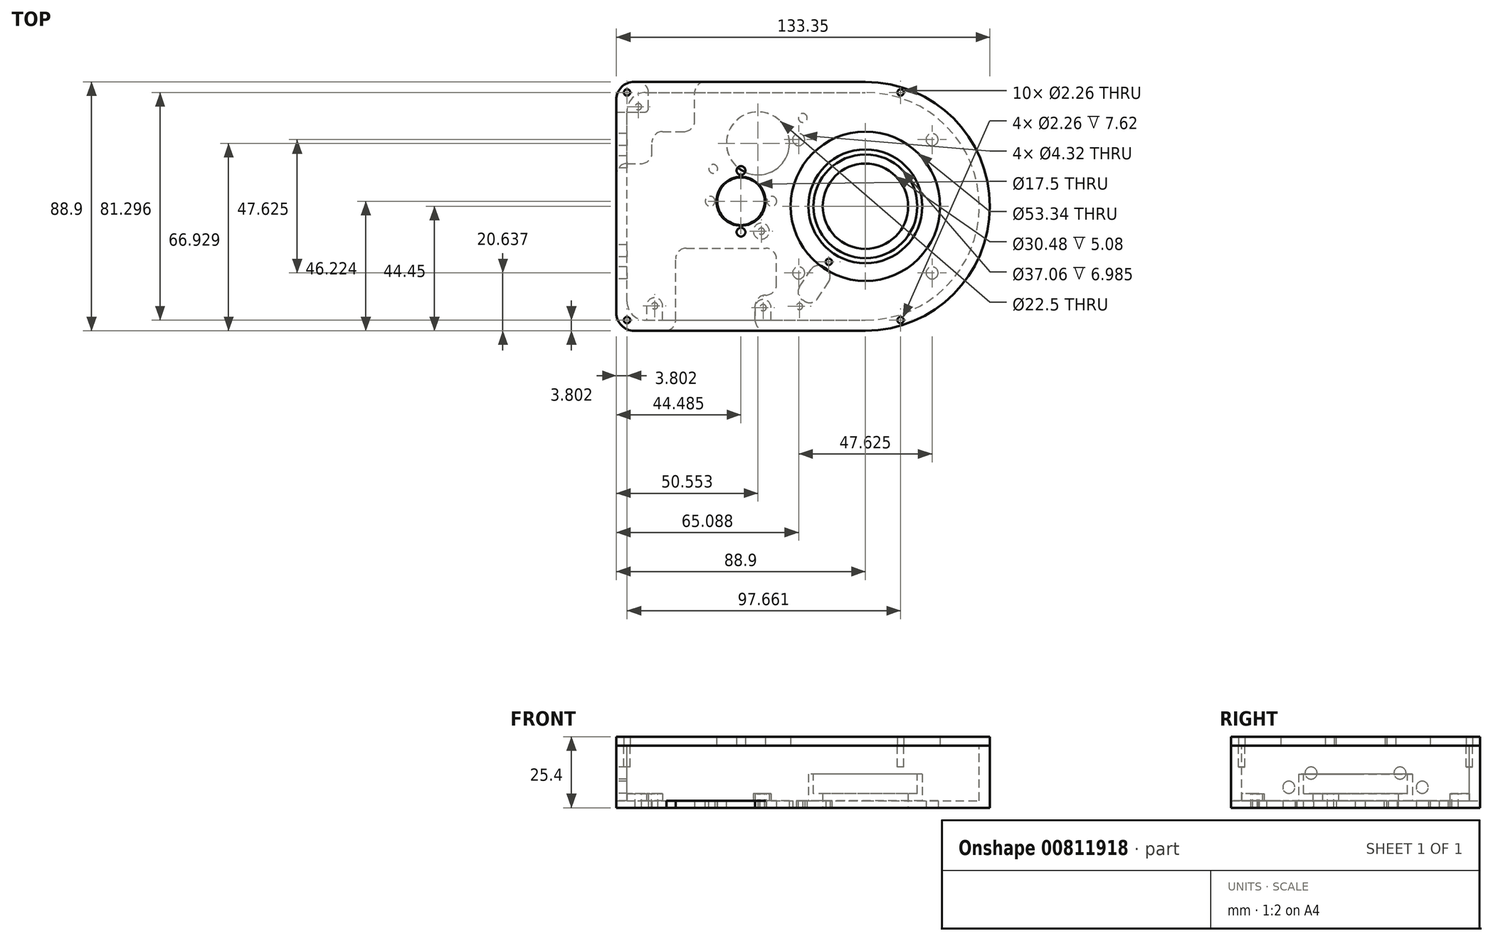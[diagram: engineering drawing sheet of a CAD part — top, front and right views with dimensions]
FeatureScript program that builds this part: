
annotation { "Feature Type Name" : "Feature", "Feature Type Description" : "" }
export const myFeature = defineFeature(function(context is Context, id is Id, definition is map)
    precondition{}
    {
        {
            var Q0;
            Q0=qCreatedBy(makeId("Top.planeOp"),FACE);
            var sketch = newSketch(context, id + "F0", { "sketchPlane" : qUnion([Q0])});
            skLineSegment(sketch, "E0.bottom", {"start": v(6.35, 0) * mm, "end": v(88.9, 0) * mm});
            skLineSegment(sketch, "E0.top", {"start": v(6.35, 88.9) * mm, "end": v(88.9, 88.9) * mm});
            skLineSegment(sketch, "E0.left", {"start": v(0, 6.35) * mm, "end": v(0, 82.55) * mm});
            skArc(sketch, "E1", {"start": v(88.9, 0) * mm, "mid": v(133.35, 44.45) * mm, "end": v(88.9, 88.9) * mm});
            skCircle(sketch, "E2", {"center": v(88.9, 44.45) * mm, "radius": 15.24 * mm});
            skPoint(sketch, "E3.visualSharp", {"position": v(0, 88.9) * mm});
            skArc(sketch, "E3.filletArc", {"start": v(6.35, 88.9) * mm, "mid": v(1.86, 87.04) * mm, "end": v(0, 82.55) * mm});
            skPoint(sketch, "E4.visualSharp", {"position": v(0, 0) * mm});
            skArc(sketch, "E4.filletArc", {"start": v(0, 6.35) * mm, "mid": v(1.86, 1.86) * mm, "end": v(6.35, 0) * mm});
            skSolve(sketch);
        }
        {
            var Q0;
            {var subQ4=sQuery(id+"F0.wireOp",EDGE,"E1");var subQ7=sQuery(id+"F0.wireOp",EDGE,"E0.bottom");Q0=qUnion([makeQuery(id+"F0.imprint","IMPRINT",FACE,{"disambiguationData":[TD([[makeQuery(id+"F0.imprint","IMPRINT",EDGE,{"derivedFrom":subQ7}),1.0]])]}),makeQuery(id+"F0.imprint","IMPRINT",FACE,{"disambiguationData":[TD([[makeQuery(id+"F0.imprint","IMPRINT",EDGE,{"derivedFrom":subQ4}),1.0]])]})]);}
            extrude(context, id + "F1", {"entities" : qUnion([Q0]), "depth" : 22.22 * mm});
        }
        {
            var Q0;
            Q0=makeQuery(id+"F1.opExtrude","CAP_FACE",FACE,{"disambiguationData":[OSD([sQuery(id+"F0.wireOp",EDGE,"E0.bottom"),sQuery(id+"F0.wireOp",EDGE,"E0.top"),sQuery(id+"F0.wireOp",EDGE,"E0.left"),sQuery(id+"F0.wireOp",EDGE,"E1"),sQuery(id+"F0.wireOp",EDGE,"E2")])],"isStart":false});
            var sketch = newSketch(context, id + "F2", { "sketchPlane" : qUnion([Q0])});
            skLineSegment(sketch, "E5.0", {"start": v(10.41, 85.1) * mm, "end": v(88.9, 85.1) * mm});
            skLineSegment(sketch, "E5.1", {"start": v(3.8, 10.41) * mm, "end": v(3.8, 78.49) * mm});
            skLineSegment(sketch, "E5.2", {"start": v(10.41, 3.8) * mm, "end": v(88.9, 3.8) * mm});
            skArc(sketch, "E5.3", {"start": v(88.9, 3.81) * mm, "mid": v(129.54, 44.45) * mm, "end": v(88.9, 85.1) * mm});
            skPoint(sketch, "E6.visualSharp", {"position": v(3.8, 85.1) * mm});
            skArc(sketch, "E6.filletArc", {"start": v(10.41, 85.1) * mm, "mid": v(5.74, 83.16) * mm, "end": v(3.8, 78.49) * mm});
            skPoint(sketch, "E7.visualSharp", {"position": v(3.8, 3.8) * mm});
            skArc(sketch, "E7.filletArc", {"start": v(3.8, 10.41) * mm, "mid": v(5.74, 5.74) * mm, "end": v(10.41, 3.8) * mm});
            skSolve(sketch);
        }
        {
            var Q0;
            {var subQ0=makeQuery(id+"F2.imprint","IMPRINT",EDGE,{"derivedFrom":makeQuery(id+"F1.opExtrude","CAP_EDGE",EDGE,{"disambiguationData":[OSD([sQuery(id+"F0.wireOp",EDGE,"E2")])],"isStart":false})});Q0=qUnion([makeQuery(id+"F2.imprint","IMPRINT",FACE,{"disambiguationData":[TD([[subQ0,1.0]])]}),makeQuery(id+"F2.imprint","IMPRINT",FACE,{"disambiguationData":[TD([[makeQuery(id+"F2.imprint","IMPRINT",EDGE,{"derivedFrom":sQuery(id+"F2.wireOp",EDGE,"E5.0")}),-1.0]])]})]);}
            extrude(context, id + "F3", {"entities" : qUnion([Q0]), "operationType" : NewBodyOperationType.REMOVE, "oppositeDirection" : true, "depth" : 19.68 * mm});
        }
        {
            var Q0;
            Q0=makeQuery(id+"F3.boolean.opBoolean","COPY",FACE,{"derivedFrom":makeQuery(id+"F3.opExtrude","CAP_FACE",FACE,{"disambiguationData":[OSD([sQuery(id+"F2.wireOp",EDGE,"E5.0"),sQuery(id+"F2.wireOp",EDGE,"E5.1"),sQuery(id+"F2.wireOp",EDGE,"E5.2"),sQuery(id+"F2.wireOp",EDGE,"E5.3"),sQuery(id+"F2.wireOp",EDGE,"E6.filletArc"),sQuery(id+"F2.wireOp",EDGE,"E7.filletArc")])],"isStart":false})});
            var sketch = newSketch(context, id + "F4", { "sketchPlane" : qUnion([Q0])});
            skArc(sketch, "E8.0", {"start": v(88.9, 3.81) * mm, "mid": v(129.54, 44.45) * mm, "end": v(88.9, 85.1) * mm, "construction": true});
            skCircle(sketch, "E9", {"center": v(88.9, 44.45) * mm, "radius": 20.32 * mm});
            skCircle(sketch, "E10.0", {"center": v(88.9, 44.45) * mm, "radius": 15.24 * mm});
            skSolve(sketch);
        }
        {
            var Q0;
            {var subQ0=makeQuery(id+"F4.imprint","IMPRINT",EDGE,{"derivedFrom":makeQuery(id+"F3.boolean.opBoolean","INTERSECT",EDGE,{"derivedFrom":[makeQuery(id+"F1.opExtrude","SWEPT_FACE",FACE,{"disambiguationData":[OSD([sQuery(id+"F0.wireOp",EDGE,"E2")])]}),makeQuery(id+"F3.opExtrude","CAP_FACE",FACE,{"disambiguationData":[OSD([sQuery(id+"F2.wireOp",EDGE,"E5.0"),sQuery(id+"F2.wireOp",EDGE,"E5.1"),sQuery(id+"F2.wireOp",EDGE,"E5.2"),sQuery(id+"F2.wireOp",EDGE,"E5.3"),sQuery(id+"F2.wireOp",EDGE,"E6.filletArc"),sQuery(id+"F2.wireOp",EDGE,"E7.filletArc")])],"isStart":false})]})});Q0=qUnion([makeQuery(id+"F4.imprint","IMPRINT",FACE,{"disambiguationData":[TD([[subQ0,1.0]])]}),makeQuery(id+"F4.imprint","IMPRINT",FACE,{"disambiguationData":[TD([[makeQuery(id+"F4.imprint","IMPRINT",EDGE,{"derivedFrom":sQuery(id+"F4.wireOp",EDGE,"E9")}),1.0]])]})]);}
            extrude(context, id + "F5", {"entities" : qUnion([Q0]), "operationType" : NewBodyOperationType.ADD, "depth" : 9.52 * mm});
        }
        {
            var Q0;
            Q0=makeQuery(id+"F5.opExtrude","CAP_FACE",FACE,{"disambiguationData":[OSD([sQuery(id+"F4.wireOp",EDGE,"E9")])],"isStart":false});
            var sketch = newSketch(context, id + "F6", { "sketchPlane" : qUnion([Q0])});
            skCircle(sketch, "E11", {"center": v(88.9, 44.45) * mm, "radius": 18.53 * mm});
            skSolve(sketch);
        }
        {
            var Q0;
            Q0=makeQuery(id+"F6.imprint","IMPRINT",FACE,{"disambiguationData":[TD([[makeQuery(id+"F6.imprint","IMPRINT",EDGE,{"derivedFrom":sQuery(id+"F6.wireOp",EDGE,"E11")}),1.0]])]});
            extrude(context, id + "F7", {"entities" : qUnion([Q0]), "operationType" : NewBodyOperationType.REMOVE, "oppositeDirection" : true, "depth" : 7 * mm});
        }
        {
            var Q0;
            Q0=makeQuery(id+"F1.opExtrude","CAP_FACE",FACE,{"disambiguationData":[OSD([sQuery(id+"F0.wireOp",EDGE,"E0.bottom"),sQuery(id+"F0.wireOp",EDGE,"E0.top"),sQuery(id+"F0.wireOp",EDGE,"E0.left"),sQuery(id+"F0.wireOp",EDGE,"E1"),sQuery(id+"F0.wireOp",EDGE,"E2")])],"isStart":false});
            var sketch = newSketch(context, id + "F8", { "sketchPlane" : qUnion([Q0])});
            skLineSegment(sketch, "E12", {"start": v(3.8, 85.1) * mm, "end": v(101.46, 85.1) * mm, "construction": true});
            skLineSegment(sketch, "E13", {"start": v(101.46, 85.1) * mm, "end": v(101.46, 3.8) * mm, "construction": true});
            skLineSegment(sketch, "E14", {"start": v(101.46, 3.8) * mm, "end": v(3.8, 3.8) * mm, "construction": true});
            skCircle(sketch, "E15", {"center": v(3.8, 85.1) * mm, "radius": 1.13 * mm});
            skCircle(sketch, "E16", {"center": v(3.8, 3.8) * mm, "radius": 1.13 * mm});
            skCircle(sketch, "E17", {"center": v(101.46, 3.8) * mm, "radius": 1.13 * mm});
            skCircle(sketch, "E18", {"center": v(101.46, 85.1) * mm, "radius": 1.13 * mm});
            skLineSegment(sketch, "E19", {"start": v(1.86, 87.04) * mm, "end": v(5.74, 83.16) * mm, "construction": true});
            skLineSegment(sketch, "E20", {"start": v(1.86, 1.86) * mm, "end": v(5.74, 5.74) * mm, "construction": true});
            skSolve(sketch);
        }
        {
            var Q0;
            {Q0=qUnion([makeQuery(id+"F8.imprint","IMPRINT",FACE,{"disambiguationData":[TD([[makeQuery(id+"F8.imprint","IMPRINT",EDGE,{"derivedFrom":sQuery(id+"F8.wireOp",EDGE,"E15")}),1.0]])]}),makeQuery(id+"F8.imprint","IMPRINT",FACE,{"disambiguationData":[TD([[makeQuery(id+"F8.imprint","IMPRINT",EDGE,{"derivedFrom":sQuery(id+"F8.wireOp",EDGE,"E16")}),1.0]])]}),makeQuery(id+"F8.imprint","IMPRINT",FACE,{"disambiguationData":[TD([[makeQuery(id+"F8.imprint","IMPRINT",EDGE,{"derivedFrom":sQuery(id+"F8.wireOp",EDGE,"E17")}),1.0]])]}),makeQuery(id+"F8.imprint","IMPRINT",FACE,{"disambiguationData":[TD([[makeQuery(id+"F8.imprint","IMPRINT",EDGE,{"derivedFrom":sQuery(id+"F8.wireOp",EDGE,"E18")}),1.0]])]})]);}
            extrude(context, id + "F9", {"entities" : qUnion([Q0]), "operationType" : NewBodyOperationType.REMOVE, "oppositeDirection" : true, "depth" : 7.62 * mm});
        }
        {
            var Q0;
            Q0=makeQuery(id+"F3.boolean.opBoolean","COPY",FACE,{"derivedFrom":makeQuery(id+"F3.opExtrude","CAP_FACE",FACE,{"disambiguationData":[OSD([sQuery(id+"F2.wireOp",EDGE,"E5.0"),sQuery(id+"F2.wireOp",EDGE,"E5.1"),sQuery(id+"F2.wireOp",EDGE,"E5.2"),sQuery(id+"F2.wireOp",EDGE,"E5.3"),sQuery(id+"F2.wireOp",EDGE,"E6.filletArc"),sQuery(id+"F2.wireOp",EDGE,"E7.filletArc")])],"isStart":false})});
            var sketch = newSketch(context, id + "F10", { "sketchPlane" : qUnion([Q0])});
            skCircle(sketch, "E21", {"center": v(88.9, 44.45) * mm, "radius": 38.1 * mm, "construction": true});
            skCircle(sketch, "E22", {"center": v(44.49, 46.26) * mm, "radius": 6.35 * mm, "construction": true});
            skCircle(sketch, "E23", {"center": v(44.49, 46.26) * mm, "radius": 8.5 * mm});
            skCircle(sketch, "E24", {"center": v(44.49, 46.26) * mm, "radius": 11 * mm, "construction": true});
            skCircle(sketch, "E25", {"center": v(33.49, 46.26) * mm, "radius": 1.75 * mm});
            skCircle(sketch, "E26", {"center": v(55.49, 46.26) * mm, "radius": 1.75 * mm});
            skCircle(sketch, "E27", {"center": v(50.55, 66.93) * mm, "radius": 11.25 * mm});
            skCircle(sketch, "E28", {"center": v(41.47, 82.91) * mm, "radius": 1.57 * mm, "construction": true});
            skCircle(sketch, "E29", {"center": v(66.54, 76.02) * mm, "radius": 1.57 * mm});
            skCircle(sketch, "E30", {"center": v(59.64, 50.95) * mm, "radius": 1.57 * mm, "construction": true});
            skCircle(sketch, "E31", {"center": v(34.57, 57.84) * mm, "radius": 1.57 * mm});
            skLineSegment(sketch, "E32", {"start": v(41.47, 82.91) * mm, "end": v(66.54, 76.02) * mm, "construction": true});
            skLineSegment(sketch, "E33", {"start": v(66.54, 76.02) * mm, "end": v(59.64, 50.95) * mm, "construction": true});
            skLineSegment(sketch, "E34", {"start": v(59.64, 50.95) * mm, "end": v(34.57, 57.84) * mm, "construction": true});
            skLineSegment(sketch, "E35", {"start": v(34.57, 57.84) * mm, "end": v(41.47, 82.91) * mm, "construction": true});
            skLineSegment(sketch, "E36", {"start": v(88.9, 44.45) * mm, "end": v(50.55, 66.93) * mm, "construction": true});
            skCircle(sketch, "E37", {"center": v(50.55, 66.93) * mm, "radius": 6.35 * mm, "construction": true});
            skLineSegment(sketch, "E38", {"start": v(54, 79.46) * mm, "end": v(47.1, 54.4) * mm, "construction": true});
            skArc(sketch, "E39", {"start": v(60.7, 49.08) * mm, "mid": v(116.89, 38.69) * mm, "end": v(61.17, 51.33) * mm, "construction": true});
            skLineSegment(sketch, "E40", {"start": v(88.9, 73.03) * mm, "end": v(60.33, 73.03) * mm, "construction": true});
            skLineSegment(sketch, "E41", {"start": v(60.33, 73.03) * mm, "end": v(60.33, 15.88) * mm, "construction": true});
            skLineSegment(sketch, "E42", {"start": v(60.33, 15.88) * mm, "end": v(88.9, 15.88) * mm, "construction": true});
            skLineSegment(sketch, "E43.bottom", {"start": v(38.32, 88.44) * mm, "end": v(72.07, 79.16) * mm, "construction": true});
            skLineSegment(sketch, "E43.top", {"start": v(29.04, 54.7) * mm, "end": v(62.79, 45.41) * mm, "construction": true});
            skLineSegment(sketch, "E43.left", {"start": v(38.32, 88.44) * mm, "end": v(29.04, 54.7) * mm, "construction": true});
            skLineSegment(sketch, "E43.right", {"start": v(72.07, 79.16) * mm, "end": v(62.79, 45.41) * mm, "construction": true});
            skLineSegment(sketch, "E44", {"start": v(38.32, 88.44) * mm, "end": v(62.79, 45.41) * mm, "construction": true});
            skCircle(sketch, "E45", {"center": v(88.9, 44.45) * mm, "radius": 22.23 * mm, "construction": true});
            skArc(sketch, "E46.trimOffspring", {"start": v(88.9, 15.88) * mm, "mid": v(117.48, 44.45) * mm, "end": v(88.9, 73.03) * mm, "construction": true});
            skArc(sketch, "E47.trimOffspring", {"start": v(60.99, 50.58) * mm, "mid": v(60.92, 50.26) * mm, "end": v(60.86, 49.95) * mm, "construction": true});
            skLineSegment(sketch, "E48", {"start": v(33.49, 46.26) * mm, "end": v(55.49, 46.26) * mm, "construction": true});
            skCircle(sketch, "E49", {"center": v(13.65, 8.89) * mm, "radius": 1.13 * mm});
            skCircle(sketch, "E50", {"center": v(7.87, 80.02) * mm, "radius": 1.13 * mm});
            skCircle(sketch, "E51", {"center": v(52.39, 8.25) * mm, "radius": 1.13 * mm});
            skCircle(sketch, "E52", {"center": v(51.75, 35.56) * mm, "radius": 1.13 * mm});
            skSolve(sketch);
        }
        {
            var Q0;
            Q0=qSketchRegion(id+"F10",true);
            extrude(context, id + "F11", {"entities" : qUnion([Q0]), "operationType" : NewBodyOperationType.REMOVE, "oppositeDirection" : true, "depth" : 25.4 * mm});
        }
        {
            var Q0;
            Q0=makeQuery(id+"F1.opExtrude","CAP_FACE",FACE,{"disambiguationData":[OSD([sQuery(id+"F0.wireOp",EDGE,"E0.bottom"),sQuery(id+"F0.wireOp",EDGE,"E0.top"),sQuery(id+"F0.wireOp",EDGE,"E0.left"),sQuery(id+"F0.wireOp",EDGE,"E1"),sQuery(id+"F0.wireOp",EDGE,"E2")])],"isStart":false});
            var sketch = newSketch(context, id + "F12", { "sketchPlane" : qUnion([Q0])});
            skLineSegment(sketch, "E53.0", {"start": v(6.35, 88.9) * mm, "end": v(88.9, 88.9) * mm});
            skLineSegment(sketch, "E54.0", {"start": v(6.35, 0) * mm, "end": v(88.9, 0) * mm});
            skCircle(sketch, "E55", {"center": v(88.9, 44.45) * mm, "radius": 26.67 * mm});
            skCircle(sketch, "E56.0", {"center": v(101.46, 85.1) * mm, "radius": 1.13 * mm});
            skCircle(sketch, "E57.0", {"center": v(101.46, 3.8) * mm, "radius": 1.13 * mm});
            skCircle(sketch, "E58", {"center": v(88.9, 44.45) * mm, "radius": 38.1 * mm, "construction": true});
            skCircle(sketch, "E59", {"center": v(44.49, 46.22) * mm, "radius": 6.35 * mm, "construction": true});
            skLineSegment(sketch, "E60", {"start": v(88.9, 44.45) * mm, "end": v(44.49, 46.22) * mm, "construction": true});
            skCircle(sketch, "E61", {"center": v(44.49, 46.22) * mm, "radius": 8.75 * mm});
            skCircle(sketch, "E62", {"center": v(44.49, 57.22) * mm, "radius": 1.57 * mm});
            skCircle(sketch, "E63", {"center": v(44.49, 35.22) * mm, "radius": 1.57 * mm});
            skCircle(sketch, "E64", {"center": v(44.49, 46.22) * mm, "radius": 11 * mm, "construction": true});
            skArc(sketch, "E65.0", {"start": v(6.35, 88.9) * mm, "mid": v(1.86, 87.04) * mm, "end": v(0, 82.55) * mm});
            skArc(sketch, "E66.0", {"start": v(88.9, 0) * mm, "mid": v(133.35, 44.45) * mm, "end": v(88.9, 88.9) * mm});
            skArc(sketch, "E67.0", {"start": v(0, 6.35) * mm, "mid": v(1.86, 1.86) * mm, "end": v(6.35, 0) * mm});
            skLineSegment(sketch, "E68.0", {"start": v(0, 6.35) * mm, "end": v(0, 82.55) * mm});
            skLineSegment(sketch, "E69", {"start": v(1.86, 87.04) * mm, "end": v(5.74, 83.16) * mm, "construction": true});
            skLineSegment(sketch, "E70", {"start": v(5.74, 5.74) * mm, "end": v(1.86, 1.86) * mm, "construction": true});
            skCircle(sketch, "E71.0", {"center": v(3.8, 3.8) * mm, "radius": 1.13 * mm});
            skCircle(sketch, "E72.0", {"center": v(3.8, 85.1) * mm, "radius": 1.13 * mm});
            skSolve(sketch);
        }
        {
            var Q0;
            Q0=qSketchRegion(id+"F12",true);
            extrude(context, id + "F13", {"entities" : qUnion([Q0]), "depth" : 3.17 * mm});
        }
        {
            var Q0;
            Q0=makeQuery(id+"F1.opExtrude","SWEPT_FACE",FACE,{"disambiguationData":[OSD([sQuery(id+"F0.wireOp",EDGE,"E0.left")])]});
            var sketch = newSketch(context, id + "F14", { "sketchPlane" : qUnion([Q0])});
            skCircle(sketch, "E73", {"center": v(-68.26, 7.3) * mm, "radius": 2.16 * mm});
            skCircle(sketch, "E74", {"center": v(-20.64, 7.3) * mm, "radius": 2.16 * mm});
            skCircle(sketch, "E75", {"center": v(-60.33, 12.38) * mm, "radius": 2.16 * mm});
            skCircle(sketch, "E76", {"center": v(-28.58, 12.38) * mm, "radius": 2.16 * mm});
            skSolve(sketch);
        }
        {
            var Q0;
            {Q0=qUnion([makeQuery(id+"F14.imprint","IMPRINT",FACE,{"disambiguationData":[TD([[makeQuery(id+"F14.imprint","IMPRINT",EDGE,{"derivedFrom":sQuery(id+"F14.wireOp",EDGE,"E73")}),1.0]])]}),makeQuery(id+"F14.imprint","IMPRINT",FACE,{"disambiguationData":[TD([[makeQuery(id+"F14.imprint","IMPRINT",EDGE,{"derivedFrom":sQuery(id+"F14.wireOp",EDGE,"E74")}),1.0]])]}),makeQuery(id+"F14.imprint","IMPRINT",FACE,{"disambiguationData":[TD([[makeQuery(id+"F14.imprint","IMPRINT",EDGE,{"derivedFrom":sQuery(id+"F14.wireOp",EDGE,"E75")}),1.0]])]}),makeQuery(id+"F14.imprint","IMPRINT",FACE,{"disambiguationData":[TD([[makeQuery(id+"F14.imprint","IMPRINT",EDGE,{"derivedFrom":sQuery(id+"F14.wireOp",EDGE,"E76")}),1.0]])]})]);}
            var Q1;
            Q1=makeQuery(id+"F3.boolean.opBoolean","COPY",FACE,{"derivedFrom":makeQuery(id+"F3.opExtrude","SWEPT_FACE",FACE,{"disambiguationData":[OSD([sQuery(id+"F2.wireOp",EDGE,"E5.1")])]})});
            extrude(context, id + "F15", {"entities" : qUnion([Q0]), "operationType" : NewBodyOperationType.REMOVE, "endBound" : BoundingType.UP_TO_SURFACE, "oppositeDirection" : true, "endBoundEntityFace" : qUnion([Q1]), "depth" : 25.4 * mm});
        }
        {
            var Q0;
            Q0=makeQuery(id+"F1.opExtrude","CAP_FACE",FACE,{"disambiguationData":[OSD([sQuery(id+"F0.wireOp",EDGE,"E0.bottom"),sQuery(id+"F0.wireOp",EDGE,"E0.top"),sQuery(id+"F0.wireOp",EDGE,"E0.left"),sQuery(id+"F0.wireOp",EDGE,"E1"),sQuery(id+"F0.wireOp",EDGE,"E2")])],"isStart":true});
            var sketch = newSketch(context, id + "F16", { "sketchPlane" : qUnion([Q0])});
            skCircle(sketch, "E77", {"center": v(88.9, -44.45) * mm, "radius": 28.57 * mm, "construction": true});
            skLineSegment(sketch, "E78.bottom", {"start": v(60.33, -73.03) * mm, "end": v(117.48, -73.03) * mm, "construction": true});
            skLineSegment(sketch, "E78.top", {"start": v(60.32, -15.88) * mm, "end": v(117.48, -15.88) * mm, "construction": true});
            skLineSegment(sketch, "E78.left", {"start": v(60.33, -73.03) * mm, "end": v(60.32, -15.88) * mm, "construction": true});
            skLineSegment(sketch, "E78.right", {"start": v(117.48, -73.03) * mm, "end": v(117.48, -15.88) * mm, "construction": true});
            skCircle(sketch, "E79", {"center": v(65.09, -68.26) * mm, "radius": 2.16 * mm});
            skCircle(sketch, "E80", {"center": v(65.09, -20.64) * mm, "radius": 2.16 * mm});
            skCircle(sketch, "E81", {"center": v(112.71, -68.26) * mm, "radius": 2.16 * mm});
            skCircle(sketch, "E82", {"center": v(112.71, -20.64) * mm, "radius": 2.16 * mm});
            skSolve(sketch);
        }
        {
            var Q0;
            Q0=qSketchRegion(id+"F16",true);
            var Q1;
            Q1=makeQuery(id+"F13.opExtrude","CAP_FACE",FACE,{"disambiguationData":[OSD([sQuery(id+"F12.wireOp",EDGE,"E53.0"),sQuery(id+"F12.wireOp",EDGE,"371c0f23-bf3c-4c9d-924d-81cc7ccb8cb1.0"),sQuery(id+"F12.wireOp",EDGE,"E54.0"),sQuery(id+"F12.wireOp",EDGE,"b96d94ff-ec1a-4b2b-9b8c-458846532635.0"),sQuery(id+"F12.wireOp",EDGE,"E55"),sQuery(id+"F12.wireOp",EDGE,"9dbae14e-cf3e-48dc-83e1-3c07a5446fda.0"),sQuery(id+"F12.wireOp",EDGE,"E56.0"),sQuery(id+"F12.wireOp",EDGE,"E57.0"),sQuery(id+"F12.wireOp",EDGE,"6b4a66af-594e-434c-8a20-dfd891153b47.0"),sQuery(id+"F12.wireOp",EDGE,"96ff90f1-4c31-4608-bf02-af5b741190fa.0"),sQuery(id+"F12.wireOp",EDGE,"29fa67b4-4cb7-4e05-8d40-356bbee7443a.0"),sQuery(id+"F12.wireOp",EDGE,"990dc6ae-2cc5-486f-b52c-50ade2096444.0")])],"isStart":true});
            extrude(context, id + "F17", {"entities" : qUnion([Q0]), "operationType" : NewBodyOperationType.REMOVE, "endBound" : BoundingType.UP_TO_BODY, "oppositeDirection" : true, "endBoundEntityBody" : qUnion([Q1]), "depth" : 25.4 * mm, "offsetDistance" : 25.4 * mm});
        }
        {
            var Q0;
            {var subQ6=sQuery(id+"F0.wireOp",EDGE,"E0.bottom");Q0=makeQuery(id+"F0.imprint","IMPRINT",FACE,{"disambiguationData":[TD([[makeQuery(id+"F0.imprint","IMPRINT",EDGE,{"derivedFrom":subQ6}),1.0]])]});}
            var sketch = newSketch(context, id + "F18", { "sketchPlane" : qUnion([Q0])});
            skCircle(sketch, "E83", {"center": v(88.9, 44.45) * mm, "radius": 19.82 * mm});
            skSolve(sketch);
        }
        {
            var Q0;
            Q0=makeQuery(id+"F3.boolean.opBoolean","COPY",FACE,{"derivedFrom":makeQuery(id+"F3.opExtrude","CAP_FACE",FACE,{"disambiguationData":[OSD([sQuery(id+"F2.wireOp",EDGE,"E5.0"),sQuery(id+"F2.wireOp",EDGE,"E5.1"),sQuery(id+"F2.wireOp",EDGE,"E5.2"),sQuery(id+"F2.wireOp",EDGE,"E5.3"),sQuery(id+"F2.wireOp",EDGE,"E6.filletArc"),sQuery(id+"F2.wireOp",EDGE,"E7.filletArc")])],"isStart":false})});
            var sketch = newSketch(context, id + "F19", { "sketchPlane" : qUnion([Q0])});
            skCircle(sketch, "E84", {"center": v(88.9, 44.45) * mm, "radius": 25.4 * mm});
            skCircle(sketch, "E85.0", {"center": v(88.9, 44.45) * mm, "radius": 15.24 * mm});
            skSolve(sketch);
        }
        {
            var Q0;
            Q0=makeQuery(id+"F0.imprint","IMPRINT",FACE,{"disambiguationData":[TD([[makeQuery(id+"F0.imprint","IMPRINT",EDGE,{"derivedFrom":sQuery(id+"F0.wireOp",EDGE,"E0.bottom")}),1.0]])]});
            var sketch = newSketch(context, id + "F20", { "sketchPlane" : qUnion([Q0])});
            skLineSegment(sketch, "E86.bottom", {"start": v(17.87, 0) * mm, "end": v(52.22, 0) * mm});
            skLineSegment(sketch, "E86.top", {"start": v(24.96, 29.46) * mm, "end": v(53.34, 29.46) * mm});
            skLineSegment(sketch, "E86.left", {"start": v(21.15, 3.77) * mm, "end": v(21.15, 25.65) * mm});
            skLineSegment(sketch, "E86.right", {"start": v(57.15, 16.51) * mm, "end": v(57.15, 25.65) * mm});
            skLineSegment(sketch, "E87", {"start": v(49.53, 3.81) * mm, "end": v(49.53, 8.9) * mm});
            skLineSegment(sketch, "E88", {"start": v(53.34, 12.7) * mm, "end": v(53.34, 12.7) * mm});
            skPoint(sketch, "E89.visualSharp", {"position": v(49.53, 12.7) * mm});
            skArc(sketch, "E89.filletArc", {"start": v(53.34, 12.7) * mm, "mid": v(50.65, 11.58) * mm, "end": v(49.53, 8.9) * mm});
            skPoint(sketch, "E90.visualSharp", {"position": v(21.15, 29.46) * mm});
            skArc(sketch, "E90.filletArc", {"start": v(24.96, 29.46) * mm, "mid": v(22.26, 28.35) * mm, "end": v(21.15, 25.65) * mm});
            skPoint(sketch, "E91.visualSharp", {"position": v(57.15, 29.46) * mm});
            skArc(sketch, "E91.filletArc", {"start": v(57.15, 25.65) * mm, "mid": v(56.03, 28.35) * mm, "end": v(53.34, 29.46) * mm});
            skPoint(sketch, "E92.visualSharp", {"position": v(57.15, 12.7) * mm});
            skArc(sketch, "E92.filletArc", {"start": v(53.34, 12.7) * mm, "mid": v(56.03, 13.82) * mm, "end": v(57.15, 16.51) * mm});
            skLineSegment(sketch, "E93", {"start": v(52.22, 0) * mm, "end": v(53.34, 0) * mm});
            skPoint(sketch, "E94.visualSharp", {"position": v(21.15, 0) * mm});
            skArc(sketch, "E94.filletArc", {"start": v(17.87, 0) * mm, "mid": v(20.21, 1.27) * mm, "end": v(21.15, 3.77) * mm});
            skPoint(sketch, "E95.visualSharp", {"position": v(49.53, 0) * mm});
            skArc(sketch, "E95.filletArc", {"start": v(49.53, 3.81) * mm, "mid": v(50.65, 1.12) * mm, "end": v(53.34, 0) * mm});
            skLineSegment(sketch, "E96.bottom", {"start": v(3.81, 59.7) * mm, "end": v(8.89, 59.7) * mm});
            skLineSegment(sketch, "E96.left", {"start": v(0, 55.88) * mm, "end": v(0, 78.1) * mm});
            skLineSegment(sketch, "E96.right", {"start": v(12.7, 63.5) * mm, "end": v(12.7, 67.31) * mm});
            skLineSegment(sketch, "E97", {"start": v(0, 78.1) * mm, "end": v(10.16, 78.1) * mm});
            skLineSegment(sketch, "E98", {"start": v(11.43, 79.38) * mm, "end": v(11.43, 85.1) * mm});
            skPoint(sketch, "E99.visualSharp", {"position": v(11.43, 78.1) * mm});
            skArc(sketch, "E99.filletArc", {"start": v(10.16, 78.1) * mm, "mid": v(11.06, 78.48) * mm, "end": v(11.43, 79.38) * mm});
            skArc(sketch, "E100.filletArc", {"start": v(11.43, 85.1) * mm, "mid": v(10.31, 87.78) * mm, "end": v(7.62, 88.9) * mm});
            skLineSegment(sketch, "E101.bottom", {"start": v(16.51, 71.12) * mm, "end": v(24.13, 71.12) * mm});
            skLineSegment(sketch, "E101.top", {"start": v(7.62, 88.9) * mm, "end": v(31.75, 88.9) * mm});
            skLineSegment(sketch, "E101.left", {"start": v(0, 71.12) * mm, "end": v(0, 78.1) * mm});
            skLineSegment(sketch, "E101.right", {"start": v(27.94, 74.93) * mm, "end": v(27.94, 85.1) * mm});
            skLineSegment(sketch, "E102", {"start": v(0, 55.88) * mm, "end": v(0, 55.88) * mm});
            skLineSegment(sketch, "E103", {"start": v(31.75, 88.9) * mm, "end": v(31.75, 88.9) * mm});
            skPoint(sketch, "E104.visualSharp", {"position": v(0, 59.7) * mm});
            skArc(sketch, "E104.filletArc", {"start": v(3.81, 59.7) * mm, "mid": v(1.12, 58.57) * mm, "end": v(0, 55.88) * mm});
            skPoint(sketch, "E105.visualSharp", {"position": v(12.7, 59.7) * mm});
            skArc(sketch, "E105.filletArc", {"start": v(8.89, 59.69) * mm, "mid": v(11.58, 60.8) * mm, "end": v(12.7, 63.5) * mm});
            skPoint(sketch, "E106.visualSharp", {"position": v(12.7, 71.12) * mm});
            skArc(sketch, "E106.filletArc", {"start": v(16.51, 71.12) * mm, "mid": v(13.82, 70) * mm, "end": v(12.7, 67.31) * mm});
            skPoint(sketch, "E107.visualSharp", {"position": v(27.94, 71.12) * mm});
            skArc(sketch, "E107.filletArc", {"start": v(24.13, 71.12) * mm, "mid": v(26.82, 72.24) * mm, "end": v(27.94, 74.93) * mm});
            skPoint(sketch, "E108.visualSharp", {"position": v(27.94, 88.9) * mm});
            skArc(sketch, "E108.filletArc", {"start": v(31.75, 88.9) * mm, "mid": v(29.06, 87.78) * mm, "end": v(27.94, 85.1) * mm});
            skLineSegment(sketch, "E109", {"start": v(88.9, 44.45) * mm, "end": v(60.98, 2.01) * mm, "construction": true});
            skLineSegment(sketch, "E110", {"start": v(65.4, 15.67) * mm, "end": v(69.45, 21.82) * mm});
            skLineSegment(sketch, "E111", {"start": v(74.03, 22.77) * mm, "end": v(74.87, 22.2) * mm});
            skLineSegment(sketch, "E112", {"start": v(75.82, 17.64) * mm, "end": v(71.77, 11.48) * mm});
            skLineSegment(sketch, "E113", {"start": v(67.2, 10.54) * mm, "end": v(66.35, 11.1) * mm});
            skPoint(sketch, "E114.visualSharp", {"position": v(71.27, 24.58) * mm});
            skArc(sketch, "E114.filletArc", {"start": v(74.03, 22.77) * mm, "mid": v(71.54, 23.24) * mm, "end": v(69.45, 21.82) * mm});
            skPoint(sketch, "E115.visualSharp", {"position": v(77.63, 20.4) * mm});
            skArc(sketch, "E115.filletArc", {"start": v(75.82, 17.64) * mm, "mid": v(76.3, 20.12) * mm, "end": v(74.87, 22.2) * mm});
            skPoint(sketch, "E116.visualSharp", {"position": v(69.95, 8.72) * mm});
            skArc(sketch, "E116.filletArc", {"start": v(67.2, 10.54) * mm, "mid": v(69.68, 10.06) * mm, "end": v(71.77, 11.48) * mm});
            skPoint(sketch, "E117.visualSharp", {"position": v(63.59, 12.91) * mm});
            skArc(sketch, "E117.filletArc", {"start": v(65.4, 15.67) * mm, "mid": v(64.93, 13.19) * mm, "end": v(66.35, 11.1) * mm});
            skCircle(sketch, "E118", {"center": v(75.85, 24.61) * mm, "radius": 1.13 * mm});
            skCircle(sketch, "E119", {"center": v(65.38, 8.7) * mm, "radius": 1.13 * mm});
            skLineSegment(sketch, "E120", {"start": v(67.43, 18.75) * mm, "end": v(73.8, 14.56) * mm, "construction": true});
            skSolve(sketch);
        }
        {
            var Q0;
            Q0=qSketchRegion(id+"F20",true);
            extrude(context, id + "F21", {"entities" : qUnion([Q0]), "operationType" : NewBodyOperationType.REMOVE, "depth" : 2.54 * mm, "offsetDistance" : 25.4 * mm});
        }
        {
            var Q0;
            Q0=makeQuery(id+"F19.imprint","IMPRINT",FACE,{"disambiguationData":[TD([[makeQuery(id+"F19.imprint","IMPRINT",EDGE,{"derivedFrom":sQuery(id+"F19.wireOp",EDGE,"E84")}),-1.0]])]});
            var sketch = newSketch(context, id + "F22", { "sketchPlane" : qUnion([Q0])});
            skLineSegment(sketch, "E121.0", {"start": v(3.8, 78.1) * mm, "end": v(10.16, 78.1) * mm});
            skPoint(sketch, "E122.0", {"position": v(11.06, 78.48) * mm});
            skArc(sketch, "E123.0", {"start": v(10.16, 78.1) * mm, "mid": v(11.06, 78.48) * mm, "end": v(11.43, 79.38) * mm});
            skLineSegment(sketch, "E124.0", {"start": v(11.43, 79.38) * mm, "end": v(11.43, 85.1) * mm});
            skArc(sketch, "E125.0", {"start": v(10.41, 85.1) * mm, "mid": v(5.74, 83.16) * mm, "end": v(3.8, 78.49) * mm});
            skLineSegment(sketch, "E126.0", {"start": v(10.41, 85.1) * mm, "end": v(11.43, 85.1) * mm});
            skLineSegment(sketch, "E127.0", {"start": v(3.8, 78.1) * mm, "end": v(3.8, 78.49) * mm});
            skCircle(sketch, "E128.0", {"center": v(51.75, 35.56) * mm, "radius": 1.13 * mm});
            skCircle(sketch, "E129.0", {"center": v(13.65, 8.89) * mm, "radius": 1.13 * mm});
            skCircle(sketch, "E130.0", {"center": v(52.39, 8.25) * mm, "radius": 1.13 * mm});
            skCircle(sketch, "E131.0", {"center": v(7.87, 80.02) * mm, "radius": 1.13 * mm});
            skCircle(sketch, "E132", {"center": v(51.75, 35.56) * mm, "radius": 2.86 * mm});
            skCircle(sketch, "E133", {"center": v(52.39, 8.25) * mm, "radius": 2.86 * mm});
            skArc(sketch, "E134", {"start": v(16.5, 8.89) * mm, "mid": v(13.65, 11.75) * mm, "end": v(10.8, 8.89) * mm});
            skLineSegment(sketch, "E135.0", {"start": v(49.53, 3.81) * mm, "end": v(49.53, 8.9) * mm, "construction": true});
            skLineSegment(sketch, "E136", {"start": v(10.8, 8.89) * mm, "end": v(10.8, 3.8) * mm});
            skLineSegment(sketch, "E137", {"start": v(10.8, 3.8) * mm, "end": v(16.5, 3.8) * mm});
            skLineSegment(sketch, "E138", {"start": v(16.5, 3.8) * mm, "end": v(16.5, 8.89) * mm});
            skLineSegment(sketch, "E139", {"start": v(49.53, 8.25) * mm, "end": v(49.53, 3.8) * mm});
            skLineSegment(sketch, "E140", {"start": v(49.53, 3.8) * mm, "end": v(55.24, 3.8) * mm});
            skLineSegment(sketch, "E141", {"start": v(55.24, 3.8) * mm, "end": v(55.24, 8.25) * mm});
            skSolve(sketch);
        }
        {
            var Q0;
            Q0=qSketchRegion(id+"F22",true);
            extrude(context, id + "F23", {"entities" : qUnion([Q0]), "operationType" : NewBodyOperationType.ADD, "depth" : 2.54 * mm, "offsetDistance" : 25.4 * mm});
        }
    });
